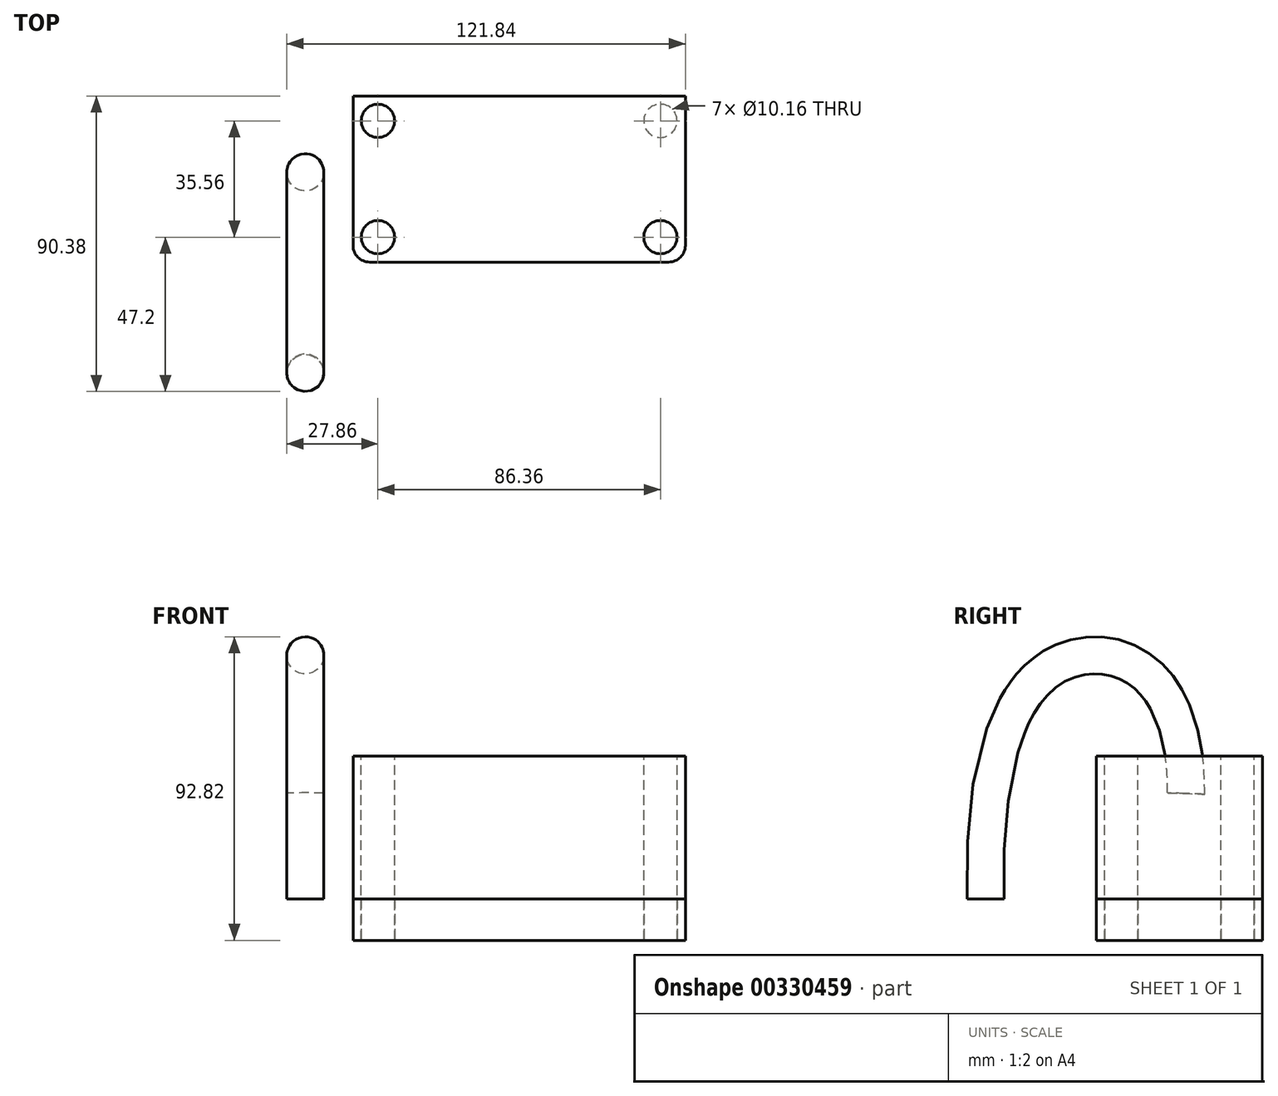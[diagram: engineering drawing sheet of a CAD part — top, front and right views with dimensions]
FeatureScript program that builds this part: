
annotation { "Feature Type Name" : "Feature", "Feature Type Description" : "" }
export const myFeature = defineFeature(function(context is Context, id is Id, definition is map)
    precondition{}
    {
        {
            var Q0;
            Q0=qCreatedBy(makeId("Top.planeOp"),FACE);
            var sketch = newSketch(context, id + "F0", { "sketchPlane" : qUnion([Q0])});
            skLineSegment(sketch, "E0.bottom", {"start": v(-50.8, 25.4) * mm, "end": v(50.8, 25.4) * mm});
            skLineSegment(sketch, "E0.top", {"start": v(-45.72, -25.4) * mm, "end": v(45.72, -25.4) * mm});
            skLineSegment(sketch, "E0.left", {"start": v(-50.8, 25.4) * mm, "end": v(-50.8, -20.32) * mm});
            skLineSegment(sketch, "E0.right", {"start": v(50.8, 25.4) * mm, "end": v(50.8, -20.32) * mm});
            skLineSegment(sketch, "E1", {"start": v(-50.8, 0) * mm, "end": v(50.8, 0) * mm, "construction": true});
            skLineSegment(sketch, "E2", {"start": v(0, 25.4) * mm, "end": v(0, -25.4) * mm, "construction": true});
            skCircle(sketch, "E3.MirrorC", {"center": v(-43.18, 17.78) * mm, "radius": 5.08 * mm});
            skPoint(sketch, "E4.visualSharp", {"position": v(-50.8, -25.4) * mm});
            skArc(sketch, "E4.filletArc", {"start": v(-50.8, -20.32) * mm, "mid": v(-49.31, -23.91) * mm, "end": v(-45.72, -25.4) * mm});
            skPoint(sketch, "E5.visualSharp", {"position": v(50.8, -25.4) * mm});
            skArc(sketch, "E5.filletArc", {"start": v(45.72, -25.4) * mm, "mid": v(49.31, -23.91) * mm, "end": v(50.8, -20.32) * mm});
            skLineSegment(sketch, "E6.MirrorCS", {"start": v(50.8, 0) * mm, "end": v(-50.8, 0) * mm, "construction": true});
            skCircle(sketch, "E7.MirrorC", {"center": v(43.18, 17.78) * mm, "radius": 5.08 * mm});
            skCircle(sketch, "E8.MirrorC", {"center": v(-43.18, -17.78) * mm, "radius": 5.08 * mm});
            skCircle(sketch, "E9.MirrorC", {"center": v(43.18, -17.78) * mm, "radius": 5.08 * mm});
            skSolve(sketch);
        }
        {
            var Q0;
            Q0=makeQuery(id+"F0.imprint","IMPRINT",FACE,{"disambiguationData":[TD([[makeQuery(id+"F0.imprint","IMPRINT",EDGE,{"derivedFrom":sQuery(id+"F0.wireOp",EDGE,"E0.bottom")}),-1.0]])]});
            extrude(context, id + "F1", {"entities" : qUnion([Q0]), "depth" : 12.7 * mm});
        }
        {
            var Q0;
            Q0=makeQuery(id+"F1.opExtrude","SWEPT_FACE",FACE,{"disambiguationData":[OSD([sQuery(id+"F0.wireOp",EDGE,"E0.left")])]});
            var sketch = newSketch(context, id + "F2", { "sketchPlane" : qUnion([Q0])});
            skLineSegment(sketch, "E10", {"start": v(-18.55, 12.7) * mm, "end": v(-18.55, 69.06) * mm});
            skSolve(sketch);
        }
        {
            var Q0;
            Q0=makeQuery(id+"F0.imprint","IMPRINT",FACE,{"disambiguationData":[TD([[makeQuery(id+"F0.imprint","IMPRINT",EDGE,{"derivedFrom":sQuery(id+"F0.wireOp",EDGE,"E3.MirrorC")}),-1.0]])]});
            var Q1;
            Q1=makeQuery(id+"F0.imprint","IMPRINT",FACE,{"disambiguationData":[TD([[makeQuery(id+"F0.imprint","IMPRINT",EDGE,{"derivedFrom":sQuery(id+"F0.wireOp",EDGE,"E7.MirrorC")}),1.0]])]});
            var Q2;
            Q2=sQuery(id+"F2.wireOp",EDGE,"E10");
            sweep(context, id + "F3", {"profiles" : qUnion([Q0, Q1]), "path" : qUnion([Q2])});
        }
        {
            var Q0;
            Q0=makeQuery(id+"F1.opExtrude","CAP_FACE",FACE,{"disambiguationData":[OSD([sQuery(id+"F0.wireOp",EDGE,"E0.bottom"),sQuery(id+"F0.wireOp",EDGE,"E0.top"),sQuery(id+"F0.wireOp",EDGE,"E0.left"),sQuery(id+"F0.wireOp",EDGE,"E0.right"),sQuery(id+"F0.wireOp",EDGE,"E4.filletArc"),sQuery(id+"F0.wireOp",EDGE,"E5.filletArc"),sQuery(id+"F0.wireOp",EDGE,"E7.MirrorC"),sQuery(id+"F0.wireOp",EDGE,"E3.MirrorC"),sQuery(id+"F0.wireOp",EDGE,"E8.MirrorC"),sQuery(id+"F0.wireOp",EDGE,"E9.MirrorC")])],"isStart":false});
            var sketch = newSketch(context, id + "F4", { "sketchPlane" : qUnion([Q0])});
            skCircle(sketch, "E11", {"center": v(-65.37, -59.22) * mm, "radius": 5.66 * mm});
            skSolve(sketch);
        }
        {
            var Q0;
            Q0=makeQuery(id+"F1.opExtrude","SWEPT_FACE",FACE,{"disambiguationData":[OSD([sQuery(id+"F0.wireOp",EDGE,"E0.right")])]});
            var sketch = newSketch(context, id + "F5", { "sketchPlane" : qUnion([Q0])});
            skFitSpline(sketch, "E12", {"points": [v(-59.14, 12.9) * mm, v(-31.57, 86.4) * mm, v(1.94, 44.7) * mm], "startDerivative": vector(-6.92, 255.11) * mm, "endDerivative": vector(-2.49, -238.72) * mm});
            skSolve(sketch);
        }
        {
            var Q0;
            Q0=makeQuery(id+"F4.imprint","IMPRINT",FACE,{"disambiguationData":[TD([[makeQuery(id+"F4.imprint","IMPRINT",EDGE,{"derivedFrom":sQuery(id+"F4.wireOp",EDGE,"E11")}),1.0]])]});
            var Q1;
            Q1=sQuery(id+"F5.wireOp",EDGE,"E12");
            sweep(context, id + "F6", {"profiles" : qUnion([Q0]), "path" : qUnion([Q1])});
        }
    });
